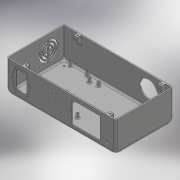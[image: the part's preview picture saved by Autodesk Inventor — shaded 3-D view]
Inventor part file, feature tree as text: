
AUTODESK INVENTOR PART (.ipt)
format: ipt  version: 2017 (Build 210142000, 142)  size: 898,048 bytes
history: native  units: mm
features: sketch x24, extrude x15, other x10, hole x8, projected_geometry x5, fillet x4, shell x1, mirror x1
ambient origin geometry x8: Origin, YZ Plane, XZ Plane, XY Plane, X Axis, Y Axis, Z Axis, Center Point
bodies: Solide1 (feature_tree)
feature tree (68):
  extrude  "Embase"  TaperAngle=0.0deg  [1 undecoded]
  fillet  "Congé1"  Radius=68.0mm
  shell  "Coque1"  Thickness=160.0mm
  extrude  "Plaque_laser+moteur"  Depth=7.0mm
  extrude  "Carte laser"  Depth=7.0mm
  extrude  "Alimentation"  Depth=7.0mm
  extrude  "Carte_electronique"  Depth=7.0mm
  extrude  "Passage_écran"  Depth=10.0mm
  extrude  "Lamage_écran"  TaperAngle=0.0deg  [1 undecoded]
  hole  "Perçage_écran"  [1 undecoded]
  hole  "Passage_potentiomètre"  [1 undecoded]
  fillet  "Congé2"  Radius=14.0mm
  hole  "Perçage_ventilateur"  [1 undecoded]
  extrude  "Lamage_plug"  Depth=59.95mm
  hole  "Perçage9"  [1 undecoded]
  extrude  "Passage_plug"  Depth=4.025mm
  extrude  "Passage laser(fenetre)"  Depth=7.0mm
  extrude  "Passage air ventillateur"  Depth=7.0mm
  extrude  "Croix passage air"  Depth=10.0mm
  extrude  "Extrution maintiens couvercle"  TaperAngle=0.0deg  [1 undecoded]
  fillet  "Congé3"  Radius=44.0mm
  hole  "Perçage maintient couvercle"  [1 undecoded]
  extrude  "Support potentiomètre"  Depth=17.5mm
  hole  "Perçage potentiomètre"  [1 undecoded]
  fillet  "Congé4"  Radius=6.0mm
  sketch  "Esquisse26"
  extrude  "Passage_écrous"  Depth=6.0mm
  other  "Plan de construction1"
  mirror  "Symétrie1"
  hole  "Perçage10"  [1 undecoded]
  hole  "Perçage11"  [1 undecoded]
  sketch  "Esquisse1"
  sketch  "Esquisse2"
  sketch  "Esquisse4"
  sketch  "Esquisse5"
  sketch  "Esquisse6"
  sketch  "Esquisse7"
  sketch  "Esquisse8"
  sketch  "Esquisse9"
  sketch  "Esquisse10"
  sketch  "Esquisse11"
  sketch  "Esquisse12"
  sketch  "Esquisse13"
  sketch  "Esquisse14"
  projected_geometry  "Boucle projetée2"
  sketch  "Esquisse18"
  sketch  "Esquisse19"
  sketch  "Esquisse21"
  sketch  "Esquisse22"
  sketch  "Esquisse23"
  projected_geometry  "Boucle projetée3"
  sketch  "Esquisse24"
  sketch  "Esquisse27"
  projected_geometry  "Boucle projetée4"
  projected_geometry  "Boucle projetée5"
  other  "Référence1"
  sketch  "Esquisse28"
  projected_geometry  "Boucle projetée6"
  other  "Référence2"
  other  "Référence4"
  sketch  "Esquisse33"
  other  "Référence5"
  sketch  "Esquisse34"
  parser-record x1  (decoder bookkeeping rows leaked as tree rows — omitted from the tree; the rows remain in map.json)
  other  "Laser_show.iam"
  other  "Plug+prise:1"
  other  "Moteur+mirroir:1"
  other  "Carte_electronique:1"
note: 11 required parameter values undecoded (feature->parameter linkage not recoverable at this tier; creation-order binding heuristic only, values carry confidence <= 0.55)
note: 1 file-system path scrubbed to <path> (originals preserved in map.json)
